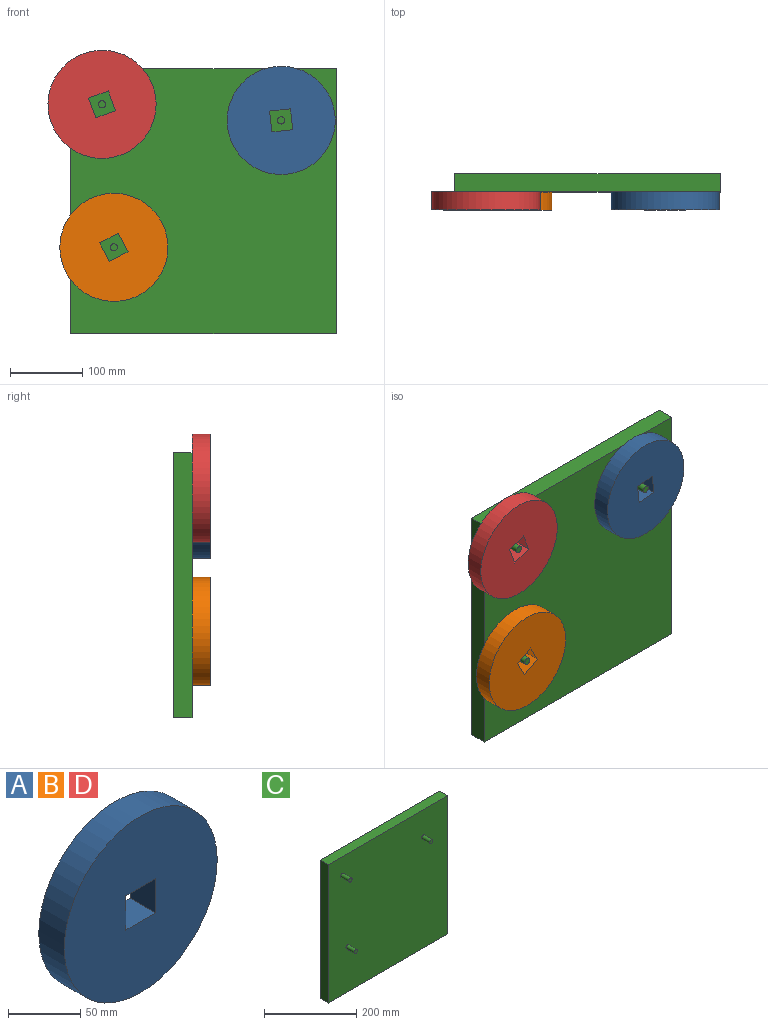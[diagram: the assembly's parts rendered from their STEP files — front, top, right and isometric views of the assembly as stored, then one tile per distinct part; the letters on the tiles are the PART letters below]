
ASSEMBLY  parts=4 mates=3
PART A: 7 faces, bbox 150x25x150 mm
  f0: plane 29.1x25mm, normal (-1,0,0), area 727.5mm2, adj f1,f3,f5,f6
  f1: plane 29.1x25mm, normal (0,0,1), area 727.5mm2, adj f0,f2,f5,f6
  f2: plane 29.1x25mm, normal (1,0,0), area 727.5mm2, adj f1,f3,f5,f6
  f3: plane 29.1x25mm, normal (0,0,-1), area 727.5mm2, adj f0,f2,f5,f6
  f4: cylinder r=75mm len=150mm, axis (0,1,0), area 11781mm2, adj f5,f6
  f5: plane 150x150mm, normal (0,-1,0), area 16824.7mm2, adj f0,f1,f2,f3,f4
  f6: plane 150x150mm, normal (0,1,0), area 16824.7mm2, adj f0,f1,f2,f3,f4
PART B: same geometry as A
PART C: 12 faces, bbox 367.6x50x367.6 mm
  f0: plane 367.62x25mm, normal (0,0,-1), area 9190.5mm2, adj f1,f3,f4,f5
  f1: plane 367.62x25mm, normal (1,0,0), area 9190.5mm2, adj f0,f2,f4,f5
  f2: plane 367.62x25mm, normal (0,0,1), area 9190.5mm2, adj f1,f3,f4,f5
  f3: plane 367.62x25mm, normal (-1,0,0), area 9190.5mm2, adj f0,f2,f4,f5
  f4: plane 367.62x367.62mm, normal (0,-1,0), area 134908.5mm2, adj f0,f1,f2,f3,f6,f8,f10
  f5: plane 367.62x367.62mm, normal (0,1,0), area 135144.2mm2, adj f0,f1,f2,f3
  f6: cylinder r=5mm len=25mm, axis (0,1,0), area 785.4mm2, adj f4,f7
  f7: plane 10x10mm, normal (0,-1,0), area 78.5mm2, adj f6
  f8: cylinder r=5mm len=25mm, axis (0,1,0), area 785.4mm2, adj f4,f9
  f9: plane 10x10mm, normal (0,-1,0), area 78.5mm2, adj f8
  f10: cylinder r=5mm len=25mm, axis (0,1,0), area 785.4mm2, adj f4,f11
  f11: plane 10x10mm, normal (0,-1,0), area 78.5mm2, adj f10
PART D: same geometry as A
PLACE A rot(axis=(0,1,0),83.9deg) t=(-152.86,-9.26,316.4)mm
PLACE B rot(axis=(0,1,0),152.3deg) t=(-13.3,-9.26,-7)mm
PLACE C t=(-183.22,-9.26,-142.59)mm fixed
PLACE D rot(axis=(0,1,0),70deg) t=(-482.56,-9.26,309.79)mm
MATE revolute D.f4 <-> C.f6  axis (0,1,0) through (-323.93,-34.26,-8.43)mm
MATE revolute A.f4 <-> C.f8  axis (0,1,0) through (-75.53,-34.26,-30.66)mm
MATE revolute B.f4 <-> C.f10  axis (0,1,0) through (-307.49,-34.26,-206.69)mm
